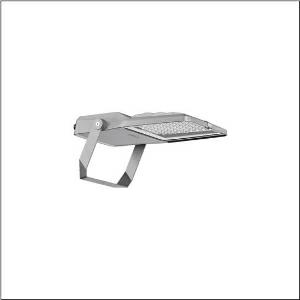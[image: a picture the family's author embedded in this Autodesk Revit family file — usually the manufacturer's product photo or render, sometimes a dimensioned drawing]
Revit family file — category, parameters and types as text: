
# Revit family: floodlight_fl_21_iq_mini___pl33t_5xa7772c2f1a_05f5
name_source: partatom
category: Lighting Fixtures
units: mm (PartAtom-declared; Revit-internal decimal feet)

## family parameters
Cut with Voids When Loaded = No
Host = Face
Light Source = No
Part Type = Normal
Room Calculation Point = No
Round Connector Dimension = Use Diameter
Shared = No

## types (1)
- --- (1 x LED, 12060 lm, 87.2 W, 3000K)
    Apparent Load = 87 VA
    CIE Flux Codes = 26 75 99 100 100
    Color Rendering = 70
    Color Temperature = 3000K
    Default Elevation = 1800 mm
    Description = Floodlight FL 21 iQ mini, floodlight, primary light control with lens, of PMMA, primary optical cover: protective disc, of toughened safety glass, transparent, light distribution: PL33T, light emission: direct distribution, installation type: surface-mounted, lamps: LED, High Power LED, rated values: 12.060lm | 87,2W | 138,3lm/W (begin service life); end service life: 12.060lm | 92,1W; at 50% lumin. flux: 6.030lm | 40,1W | 150,4lm/W, colour temperature: 3000K, colour rendering: CRI > 70, light colour: 730, light setting 1 begin service life: 100% | 12.060lm | 87,2W | 138,3lm/W | 3.000K, light setting 1 end service life: 92,1W, further light settings possible, control: Street-Remote, Auto-Match, Temp-Guard, Night-Set, Smart-Wire, Desk-Remote (wireless, voltage-free reading and setting of iQ features in the workshop via application-optimized NFC function/RFID function), optimised constant luminous flux control (CLO 2.0), pre-setting: linear dimming characteristic, with terminal, 6-pole, mains connection: 220..240V, AC, 50/60Hz, luminaire housing, of diecast aluminium, powder-coated, SITECO metallic grey (DB 702S), corrosivity category C5 mid according to DIN EN ISO 12944suitable for swimming poolschlorine-resistant, sealing non-destructively replaceable, mounting bracket, of steel, galvanised, powder-coated, SITECO metallic grey (DB 702S), protection rating (complete): IP66, insulation class (complete): insulation class II (safety insulation), certification: CE, ENEC, VDE, protection symbol: D, impact resistance: IK08, permissible operating ambient temperature: -40..+40°C, permissible operating ambient temperature for outdoor applications: -40..+50°C, standard: DIN EN 12944, LABS conformity tested according to VDMA 24364:2018-05, packaging unit: 1 piece

Light Distribution: PL33T
    Height = 70 mm
    Lamp = 1 x LED
    Lamp Light Flux = 12060 lm
    Lamp Power = 87.2 W
    Lamp count = 1
    Length = 485 mm
    Luminous efficacy = 138 lm/W
    Manufacturer = Siteco
    ModVariant = No
    Model = 5XA7772C2F1A
    Number of Poles = 1
    OnlyDefault = Yes
    Power Factor = 1
    Product Name = Floodlight FL 21 iQ mini | PL33T
    Product group = floodlight | pylon annexe
    ProductGroupID = 6201
    Protection Class = Protection class II
    Protection Degree = IP 66
    RLX_Detail_Level = 1
    RLX_Emergency_Light_Flux = 0 lm
    RLX_Emergency_Type = 0
    RLX_Emergency_Type_DB = No
    RlxData = <blob elided: 96405 chars, md5=5c8a206f>
    Socket = socket
    Standby Power = 0 W
    System Light Flux = 12060 lm
    System Power = 87 W
    Type Comments = factory setting: luminous flux: 100 % | dim-lin: 254 | 456 mA
    Type Image = l_1006845.jpg
    URL = http://relux.com
    VarID = @adj_149059
    Voltage = 0 V
    Weight = 0.00 kg
    Width = 337 mm

## geometry (parser evidence)
native form markers: Blend x4, Sweep x13
no freeform markers — native parametric forms only
